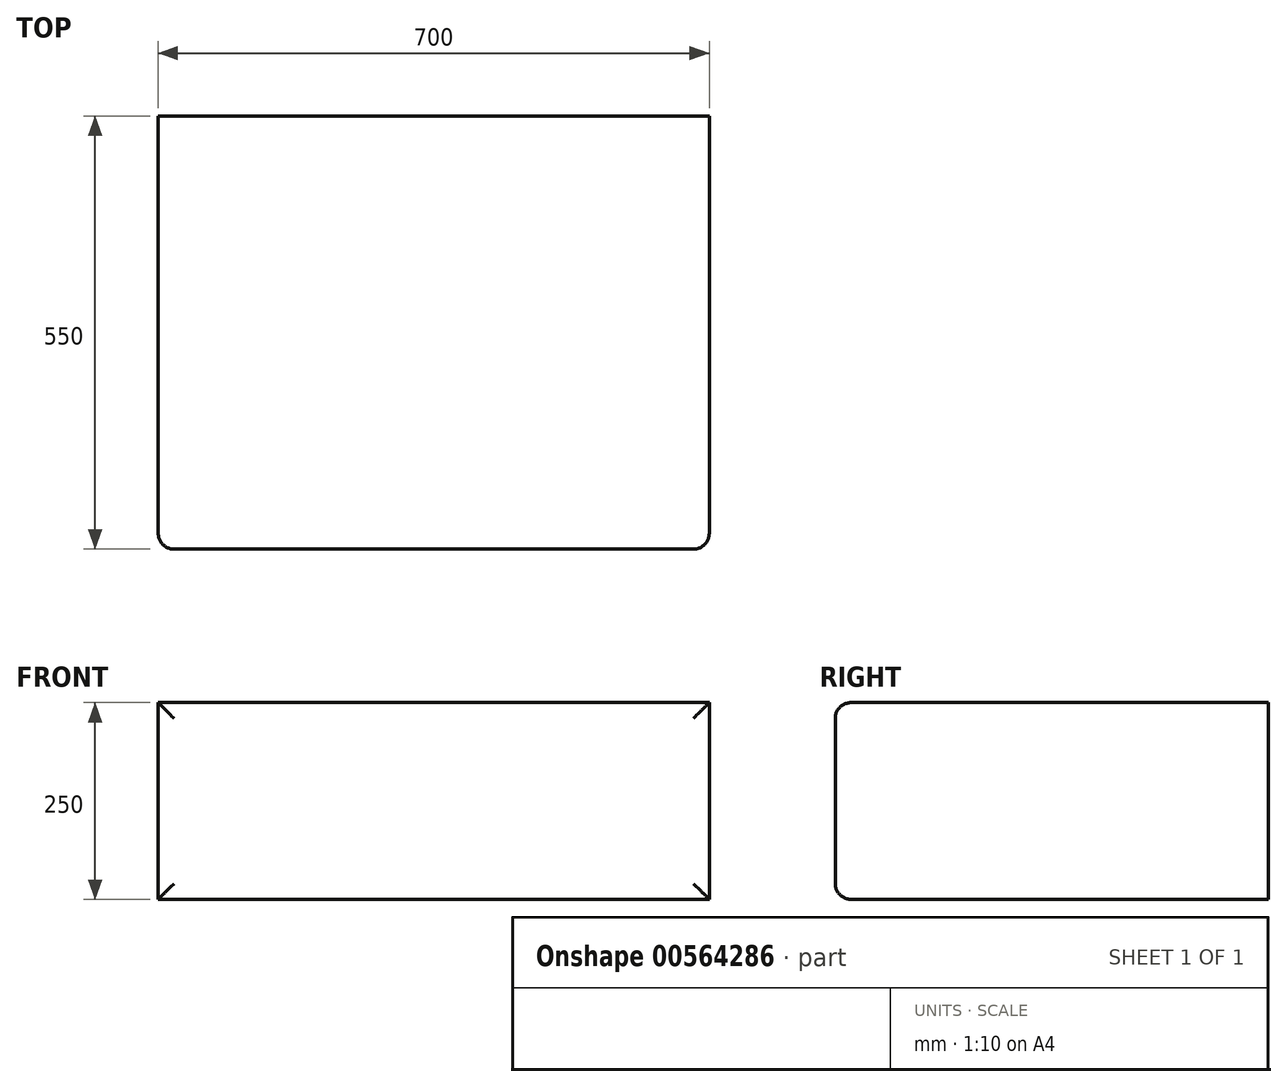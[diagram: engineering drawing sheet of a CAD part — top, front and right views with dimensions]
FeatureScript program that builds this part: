
annotation { "Feature Type Name" : "Feature", "Feature Type Description" : "" }
export const myFeature = defineFeature(function(context is Context, id is Id, definition is map)
    precondition{}
    {
        {
            var Q0;
            Q0=qCreatedBy(makeId("Front.planeOp"),FACE);
            var sketch = newSketch(context, id + "F0", { "sketchPlane" : qUnion([Q0])});
            skLineSegment(sketch, "E0.bottom", {"start": v(-340.84, -23.3) * mm, "end": v(359.16, -23.3) * mm});
            skLineSegment(sketch, "E0.top", {"start": v(-340.84, -273.3) * mm, "end": v(359.16, -273.3) * mm});
            skLineSegment(sketch, "E0.left", {"start": v(-340.84, -23.3) * mm, "end": v(-340.84, -273.3) * mm});
            skLineSegment(sketch, "E0.right", {"start": v(359.16, -23.3) * mm, "end": v(359.16, -273.3) * mm});
            skSolve(sketch);
        }
        {
            var Q0;
            Q0=makeQuery(id+"F0.imprint","IMPRINT",FACE,{"disambiguationData":[TD([[makeQuery(id+"F0.imprint","IMPRINT",EDGE,{"derivedFrom":sQuery(id+"F0.wireOp",EDGE,"E0.bottom")}),-1.0]])]});
            extrude(context, id + "F1", {"entities" : qUnion([Q0]), "depth" : 550 * mm, "offsetDistance" : 25 * mm});
        }
        {
            var Q0;
            Q0=makeQuery(id+"F1.opExtrude","CAP_EDGE",EDGE,{"disambiguationData":[OSD([sQuery(id+"F0.wireOp",EDGE,"E0.top")])],"isStart":false});
            var Q1;
            Q1=makeQuery(id+"F1.opExtrude","CAP_EDGE",EDGE,{"disambiguationData":[OSD([sQuery(id+"F0.wireOp",EDGE,"E0.bottom")])],"isStart":false});
            var Q2;
            Q2=makeQuery(id+"F1.opExtrude","CAP_EDGE",EDGE,{"disambiguationData":[OSD([sQuery(id+"F0.wireOp",EDGE,"E0.right")])],"isStart":false});
            var Q3;
            Q3=makeQuery(id+"F1.opExtrude","CAP_EDGE",EDGE,{"disambiguationData":[OSD([sQuery(id+"F0.wireOp",EDGE,"E0.left")])],"isStart":false});
            fillet(context, id + "F2", {"entities" : qUnion([Q0, Q1, Q2, Q3]), "radius" : 20 * mm, "tangentPropagation" : true, "allowEdgeOverflow" : false});
        }
    });
